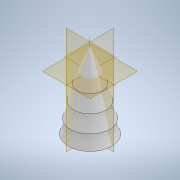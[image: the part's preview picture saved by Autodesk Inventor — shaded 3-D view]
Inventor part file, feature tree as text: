
AUTODESK INVENTOR PART (.ipt)
format: ipt  version: 2022.4 (Build 264492010, 492A)  size: 141,824 bytes
history: native  units: mm
features: revolve x1, sketch x1
ambient origin geometry x8: Origin, YZ Plane, XZ Plane, XY Plane, X Axis, Y Axis, Z Axis, Center Point
bodies: Body1 (feature_tree)
feature tree (2):
  revolve  "Revolution2"  [1 undecoded]
  sketch  "Sketch1"  dims[d0=70.0mm d1=40.0mm d2=20.0mm d3=50.0mm d4=10.0mm d5=5.0mm d6=5.0mm d8=15.0mm d9=15.0mm d10=90.0deg]
note: 1 required parameter value undecoded (feature->parameter linkage not recoverable at this tier; creation-order binding heuristic only, values carry confidence <= 0.55)
